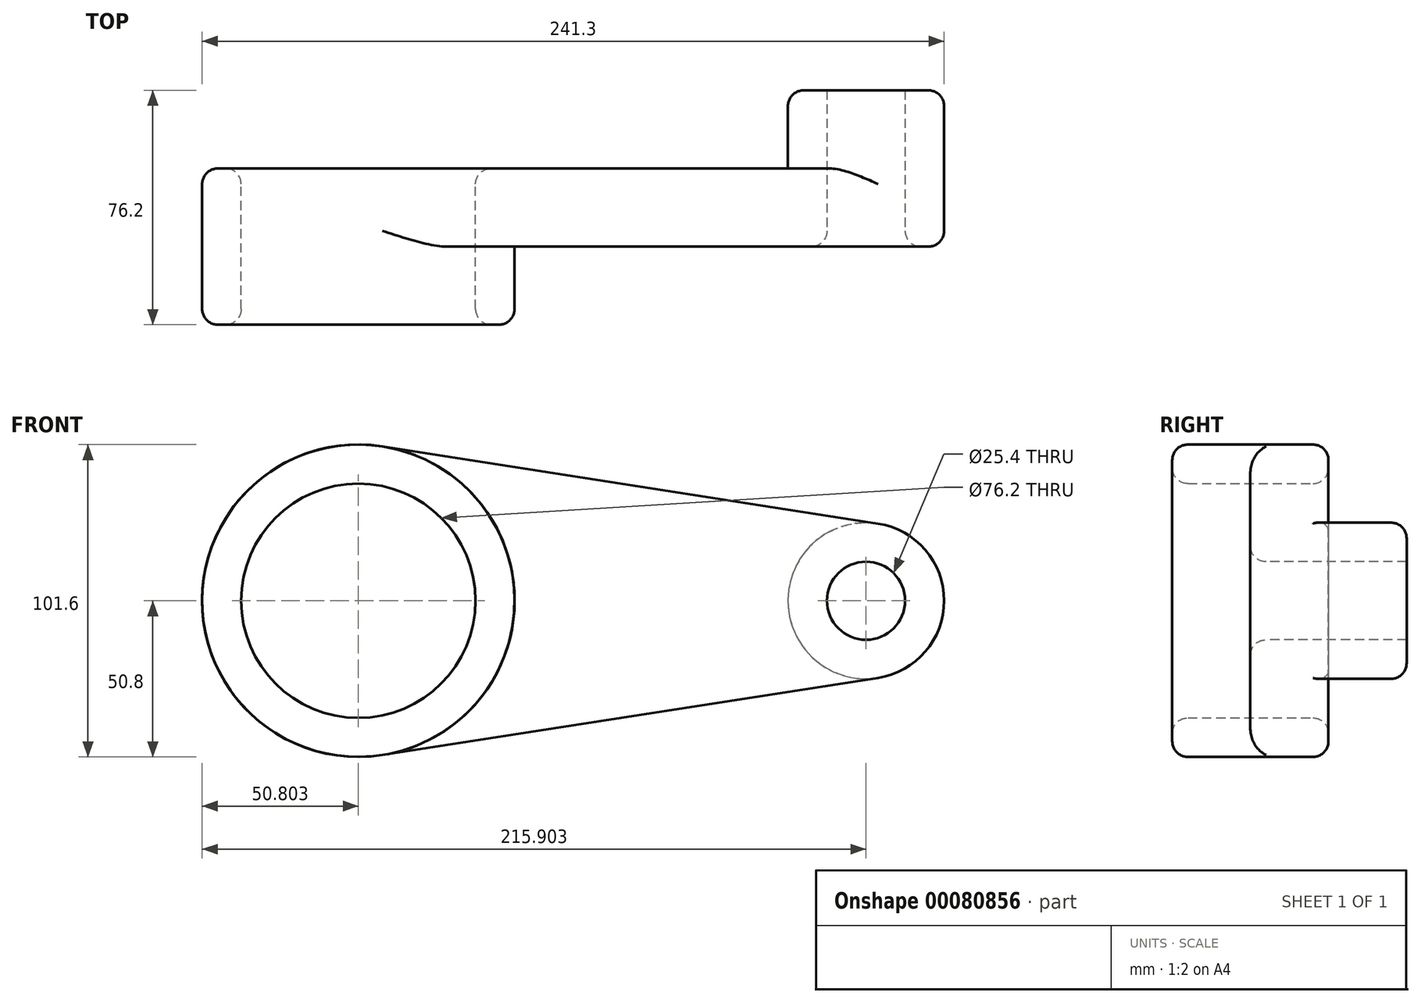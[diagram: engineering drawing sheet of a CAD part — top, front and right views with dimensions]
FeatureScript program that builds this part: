
annotation { "Feature Type Name" : "Feature", "Feature Type Description" : "" }
export const myFeature = defineFeature(function(context is Context, id is Id, definition is map)
    precondition{}
    {
        {
            var Q0;
            Q0=qCreatedBy(makeId("Front.planeOp"),FACE);
            var sketch = newSketch(context, id + "F0", { "sketchPlane" : qUnion([Q0])});
            skCircle(sketch, "E0", {"center": v(-58.2, 0) * mm, "radius": 50.8 * mm});
            skCircle(sketch, "E1", {"center": v(106.9, 0) * mm, "radius": 25.4 * mm});
            skLineSegment(sketch, "E2", {"start": v(-50.4, 50.2) * mm, "end": v(110.8, 25.1) * mm});
            skLineSegment(sketch, "E3", {"start": v(110.8, -25.1) * mm, "end": v(-50.4, -50.2) * mm});
            skCircle(sketch, "E4", {"center": v(-58.2, 0) * mm, "radius": 38.1 * mm});
            skCircle(sketch, "E5", {"center": v(106.9, 0) * mm, "radius": 12.7 * mm});
            skSolve(sketch);
        }
        {
            var Q0;
            Q0=makeQuery(id+"F0.imprint","IMPRINT",FACE,{"disambiguationData":[TD([[makeQuery(id+"F0.imprint","IMPRINT",EDGE,{"derivedFrom":sQuery(id+"F0.wireOp",EDGE,"E5")}),-1.0]])]});
            extrude(context, id + "F1", {"entities" : qUnion([Q0]), "oppositeDirection" : true, "depth" : 25.4 * mm});
        }
        {
            var Q0;
            {var subQ0=sQuery(id+"F0.wireOp",EDGE,"E2");Q0=makeQuery(id+"F0.imprint","IMPRINT",FACE,{"disambiguationData":[TD([[makeQuery(id+"F0.imprint","IMPRINT",EDGE,{"derivedFrom":subQ0}),-1.0]])]});}
            var Q1;
            Q1=makeQuery(id+"F1.opExtrude","CAP_FACE",FACE,{"disambiguationData":[OSD([sQuery(id+"F0.wireOp",EDGE,"E1"),sQuery(id+"F0.wireOp",EDGE,"E5")])],"isStart":true});
            extrude(context, id + "F2", {"entities" : qUnion([Q0, Q1]), "operationType" : NewBodyOperationType.ADD, "depth" : 25.4 * mm});
        }
        {
            var Q0;
            Q0=makeQuery(id+"F0.imprint","IMPRINT",FACE,{"disambiguationData":[TD([[makeQuery(id+"F0.imprint","IMPRINT",EDGE,{"derivedFrom":sQuery(id+"F0.wireOp",EDGE,"E4")}),-1.0]])]});
            extrude(context, id + "F3", {"entities" : qUnion([Q0]), "operationType" : NewBodyOperationType.ADD, "depth" : 50.8 * mm});
        }
        {
            var Q0;
            Q0=makeQuery(id+"F2.opExtrude","CAP_EDGE",EDGE,{"disambiguationData":[OSD([sQuery(id+"F0.wireOp",EDGE,"E0")])],"isStart":false});
            var Q1;
            Q1=makeQuery(id+"F2.opExtrude","CAP_EDGE",EDGE,{"disambiguationData":[OSD([sQuery(id+"F0.wireOp",EDGE,"E3")])],"isStart":false});
            var Q2;
            Q2=makeQuery(id+"F3.opExtrude","CAP_EDGE",EDGE,{"disambiguationData":[OSD([sQuery(id+"F0.wireOp",EDGE,"E0")])],"isStart":false});
            fillet(context, id + "F4", {"entities" : qUnion([Q0, Q1, Q2]), "radius" : 5.08 * mm, "tangentPropagation" : true, "allowEdgeOverflow" : false});
        }
        {
            var Q0;
            Q0=makeQuery(id+"F3.opExtrude","CAP_EDGE",EDGE,{"disambiguationData":[OSD([sQuery(id+"F0.wireOp",EDGE,"E4")])],"isStart":false});
            var Q1;
            Q1=makeQuery(id+"F2.opExtrude","CAP_EDGE",EDGE,{"disambiguationData":[OSD([sQuery(id+"F0.wireOp",EDGE,"E5")])],"isStart":false});
            var Q2;
            Q2=makeQuery(id+"F2.opExtrude","CAP_EDGE",EDGE,{"disambiguationData":[OSD([sQuery(id+"F0.wireOp",EDGE,"E2")])],"isStart":true});
            var Q3;
            Q3=makeQuery(id+"F3.opExtrude","CAP_EDGE",EDGE,{"disambiguationData":[OSD([sQuery(id+"F0.wireOp",EDGE,"E4")])],"isStart":true});
            var Q4;
            Q4=makeQuery(id+"F3.opExtrude","CAP_EDGE",EDGE,{"disambiguationData":[OSD([sQuery(id+"F0.wireOp",EDGE,"E0")])],"isStart":true});
            var Q5;
            Q5=makeQuery(id+"F1.opExtrude","CAP_EDGE",EDGE,{"disambiguationData":[OSD([sQuery(id+"F0.wireOp",EDGE,"E1")])],"isStart":false});
            fillet(context, id + "F5", {"entities" : qUnion([Q0, Q1, Q2, Q3, Q4, Q5]), "radius" : 5.08 * mm, "tangentPropagation" : true, "allowEdgeOverflow" : false});
        }
    });
